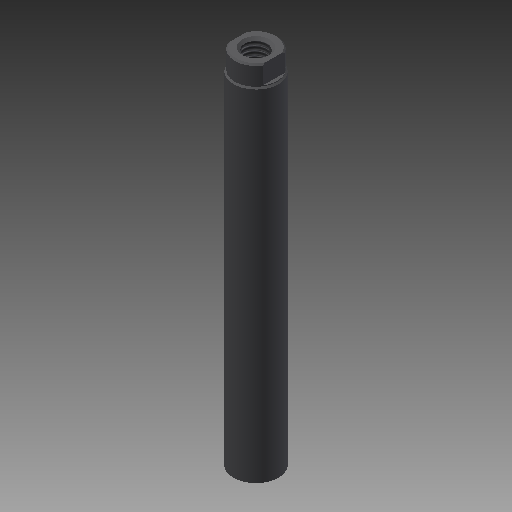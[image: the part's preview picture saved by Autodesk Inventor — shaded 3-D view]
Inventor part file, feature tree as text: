
AUTODESK INVENTOR PART (.ipt)
format: ipt  version: 2017 (Build 210142000, 142)  size: 148,480 bytes
history: native  units: in
note: dims shown in document units (in); Inventor stores cm internally (conversion verified against a paired STEP export)
features: other x98, sketch x3, revolve x1, hole x1, extrude x1
ambient origin geometry x8: Origin, YZ Plane, XZ Plane, XY Plane, X Axis, Y Axis, Z Axis, Center Point
bodies: Solid1 (feature_tree)
feature tree (104):
  revolve  "Revolution1"  [1 undecoded]
  hole  "Hole1"  [1 undecoded]
  extrude  "Extrusion1"  [1 undecoded]
  other  "b11_XY"
  other  "b11_YZ"
  other  "b11_ZX"
  other  "b11_X"
  other  "b11_Y"
  other  "b11_Z"
  other  "b11_Center"
  other  "b2_XY"
  other  "b2_YZ"
  other  "b2_ZX"
  other  "b2_X"
  other  "b2_Y"
  other  "b2_Z"
  other  "b2_Center"
  other  "f1_XY"
  other  "f1_YZ"
  other  "f1_ZX"
  other  "f1_X"
  other  "f1_Y"
  other  "f1_Z"
  other  "f1_Center"
  other  "f2_XY"
  other  "f2_YZ"
  other  "f2_ZX"
  other  "f2_X"
  other  "f2_Y"
  other  "f2_Z"
  other  "f2_Center"
  other  "h1_XY"
  other  "h1_YZ"
  other  "h1_ZX"
  other  "h1_X"
  other  "h1_Y"
  other  "h1_Z"
  other  "h1_Center"
  other  "h2_XY"
  other  "h2_YZ"
  other  "h2_ZX"
  other  "h2_X"
  other  "h2_Y"
  other  "h2_Z"
  other  "h2_Center"
  other  "npt1_XY"
  other  "npt1_YZ"
  other  "npt1_ZX"
  other  "npt1_X"
  other  "npt1_Y"
  other  "npt1_Z"
  other  "npt1_Center"
  other  "npt2_XY"
  other  "npt2_YZ"
  other  "npt2_ZX"
  other  "npt2_X"
  other  "npt2_Y"
  other  "npt2_Z"
  other  "npt2_Center"
  other  "rod_XY"
  other  "rod_YZ"
  other  "rod_ZX"
  other  "rod_X"
  other  "rod_Y"
  other  "rod_Z"
  other  "rod_Center"
  other  "rod_to_part_XY"
  other  "rod_to_part_YZ"
  other  "rod_to_part_ZX"
  other  "rod_to_part_X"
  other  "rod_to_part_Y"
  other  "rod_to_part_Z"
  other  "rod_to_part_Center"
  other  "th1_XY"
  other  "th1_YZ"
  other  "th1_ZX"
  other  "th1_X"
  other  "th1_Y"
  other  "th1_Z"
  other  "th1_Center"
  other  "th2_XY"
  other  "th2_YZ"
  other  "th2_ZX"
  other  "th2_X"
  other  "th2_Y"
  other  "th2_Z"
  other  "th2_Center"
  other  "to_rod_pivot_XY"
  other  "to_rod_pivot_YZ"
  other  "to_rod_pivot_ZX"
  other  "to_rod_pivot_X"
  other  "to_rod_pivot_Y"
  other  "to_rod_pivot_Z"
  other  "to_rod_pivot_Center"
  other  "to_rod_pivot1_XY"
  other  "to_rod_pivot1_YZ"
  other  "to_rod_pivot1_ZX"
  other  "to_rod_pivot1_X"
  other  "to_rod_pivot1_Y"
  other  "to_rod_pivot1_Z"
  other  "to_rod_pivot1_Center"
  sketch  "Sketch_31"  dims[d10=0.0in d11=0.0in d12=0.0in d13=0.0in d14=0.0in d15=0.0in d16=0.0in d17=0.0in]
  sketch  "Sketch2"  dims[d0=360.0deg]
  sketch  "Sketch_29"  dims[d1=0.156in d2=0.4769in d3=0.19in d4=0.25in d5=90.0deg d6=0.5089in d7=120.0deg d8=0.13in d9=0.0in]
note: 3 required parameter values undecoded (feature->parameter linkage not recoverable at this tier; creation-order binding heuristic only, values carry confidence <= 0.55)